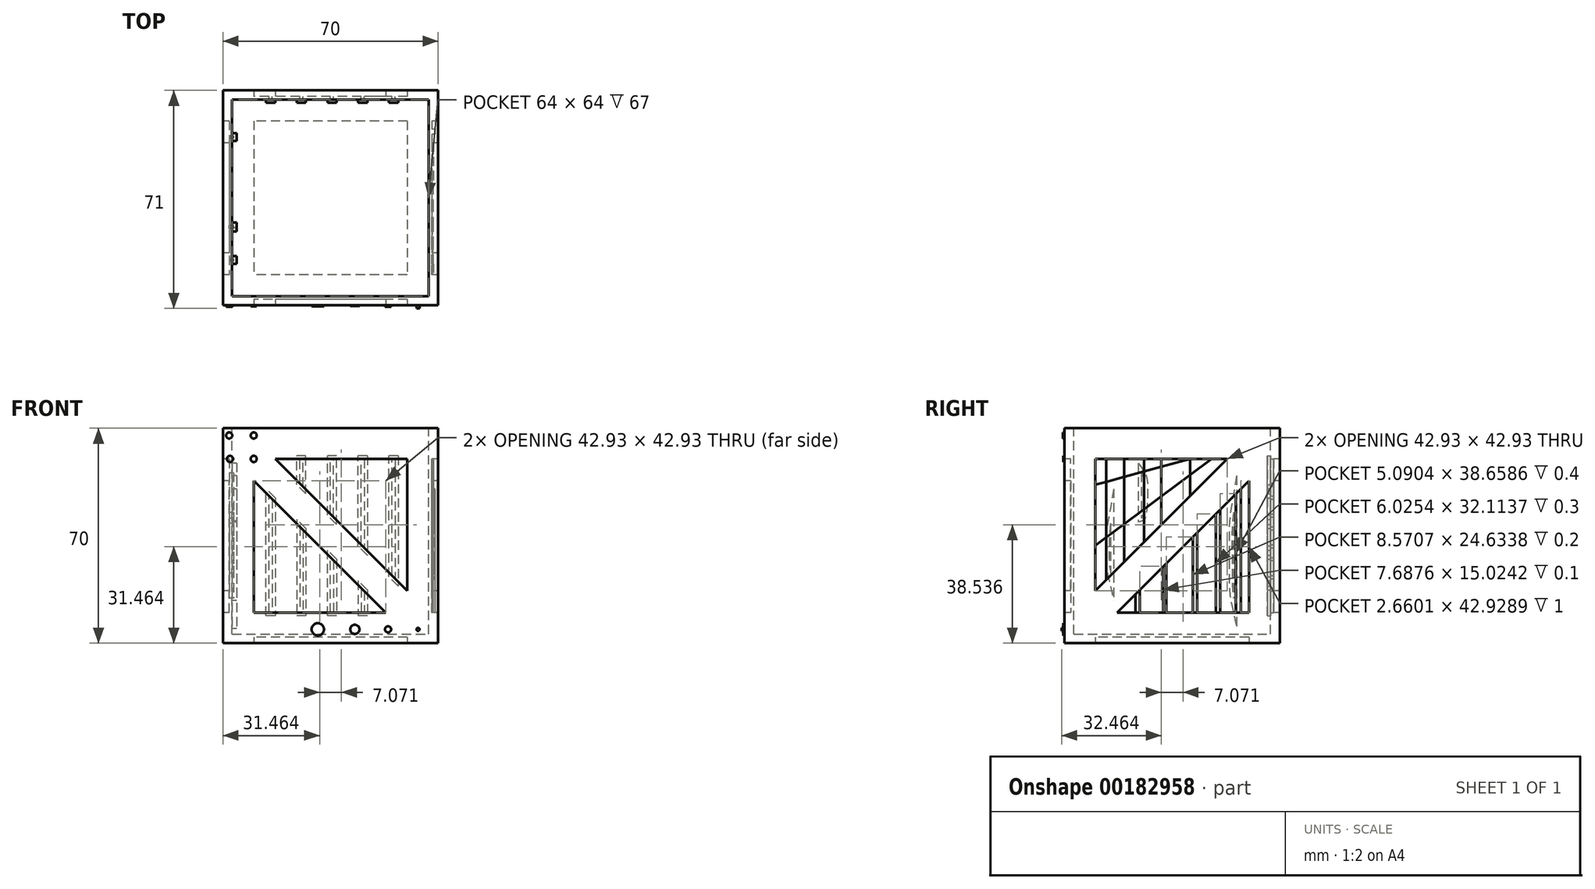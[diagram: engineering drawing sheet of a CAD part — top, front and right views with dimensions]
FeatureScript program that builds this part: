
annotation { "Feature Type Name" : "Feature", "Feature Type Description" : "" }
export const myFeature = defineFeature(function(context is Context, id is Id, definition is map)
    precondition{}
    {
        {
            var Q0;
            Q0=qCreatedBy(makeId("Top.planeOp"),FACE);
            var sketch = newSketch(context, id + "F0", { "sketchPlane" : qUnion([Q0])});
            skLineSegment(sketch, "E0.bottom", {"start": v(35, 35) * mm, "end": v(-35, 35) * mm});
            skLineSegment(sketch, "E0.top", {"start": v(35, -35) * mm, "end": v(-35, -35) * mm});
            skLineSegment(sketch, "E0.left", {"start": v(35, 35) * mm, "end": v(35, -35) * mm});
            skLineSegment(sketch, "E0.right", {"start": v(-35, 35) * mm, "end": v(-35, -35) * mm});
            skPoint(sketch, "E0.middle", {"position": v(0, 0) * mm});
            skLineSegment(sketch, "E1.0", {"start": v(25, 25) * mm, "end": v(-25, 25) * mm});
            skLineSegment(sketch, "E1.1", {"start": v(25, 25) * mm, "end": v(25, -25) * mm});
            skLineSegment(sketch, "E1.2", {"start": v(25, -25) * mm, "end": v(-25, -25) * mm});
            skLineSegment(sketch, "E1.3", {"start": v(-25, 25) * mm, "end": v(-25, -25) * mm});
            skLineSegment(sketch, "E2.0", {"start": v(33, 33) * mm, "end": v(-33, 33) * mm});
            skLineSegment(sketch, "E2.1", {"start": v(33, 33) * mm, "end": v(33, -33) * mm});
            skLineSegment(sketch, "E2.2", {"start": v(33, -33) * mm, "end": v(-33, -33) * mm});
            skLineSegment(sketch, "E2.3", {"start": v(-33, 33) * mm, "end": v(-33, -33) * mm});
            skSolve(sketch);
        }
        {
            var Q0;
            Q0=makeQuery(id+"F0.imprint","IMPRINT",FACE,{"disambiguationData":[TD([[makeQuery(id+"F0.imprint","IMPRINT",EDGE,{"derivedFrom":sQuery(id+"F0.wireOp",EDGE,"E1.0")}),-1.0]])]});
            extrude(context, id + "F1", {"entities" : qUnion([Q0]), "depth" : 2 * mm});
        }
        {
            var Q0;
            Q0=makeQuery(id+"F0.imprint","IMPRINT",FACE,{"disambiguationData":[TD([[makeQuery(id+"F0.imprint","IMPRINT",EDGE,{"derivedFrom":sQuery(id+"F0.wireOp",EDGE,"E0.bottom")}),1.0]])]});
            extrude(context, id + "F2", {"entities" : qUnion([Q0]), "operationType" : NewBodyOperationType.ADD, "depth" : 70 * mm});
        }
        {
            var Q0;
            Q0=makeQuery(id+"F2.opExtrude","SWEPT_FACE",FACE,{"disambiguationData":[OSD([sQuery(id+"F0.wireOp",EDGE,"E0.top")])]});
            var sketch = newSketch(context, id + "F3", { "sketchPlane" : qUnion([Q0])});
            skLineSegment(sketch, "E3.0", {"start": v(35, 0) * mm, "end": v(-35, 0) * mm});
            skLineSegment(sketch, "E4.0", {"start": v(35, 70) * mm, "end": v(35, 0) * mm});
            skLineSegment(sketch, "E5.0", {"start": v(-35, 70) * mm, "end": v(-35, 0) * mm});
            skLineSegment(sketch, "E6.0", {"start": v(35, 70) * mm, "end": v(-35, 70) * mm});
            skLineSegment(sketch, "E7.0", {"start": v(25, 10) * mm, "end": v(-25, 10) * mm});
            skLineSegment(sketch, "E7.1", {"start": v(25, 60) * mm, "end": v(25, 10) * mm});
            skLineSegment(sketch, "E7.2", {"start": v(25, 60) * mm, "end": v(-25, 60) * mm});
            skLineSegment(sketch, "E7.3", {"start": v(-25, 60) * mm, "end": v(-25, 10) * mm});
            skLineSegment(sketch, "E8", {"start": v(35, 0) * mm, "end": v(-35, 70) * mm, "construction": true});
            skLineSegment(sketch, "E9.0", {"start": v(17.93, 10) * mm, "end": v(-25, 52.93) * mm});
            skLineSegment(sketch, "E10.trimOffspring", {"start": v(25, 17.07) * mm, "end": v(-17.93, 60) * mm});
            skSolve(sketch);
        }
        {
            var Q0;
            {var subQ3=sQuery(id+"F3.wireOp",EDGE,"E10.trimOffspring");Q0=makeQuery(id+"F3.imprint","IMPRINT",FACE,{"disambiguationData":[TD([[makeQuery(id+"F3.imprint","IMPRINT",EDGE,{"derivedFrom":subQ3}),-1.0]])]});}
            var Q1;
            {var subQ3=sQuery(id+"F3.wireOp",EDGE,"E9.0");Q1=makeQuery(id+"F3.imprint","IMPRINT",FACE,{"disambiguationData":[TD([[makeQuery(id+"F3.imprint","IMPRINT",EDGE,{"derivedFrom":subQ3}),1.0]])]});}
            extrude(context, id + "F4", {"entities" : qUnion([Q0, Q1]), "operationType" : NewBodyOperationType.REMOVE, "endBound" : BoundingType.THROUGH_ALL, "oppositeDirection" : true, "depth" : 25 * mm});
        }
        {
            var Q0;
            Q0=makeQuery(id+"F2.opExtrude","SWEPT_FACE",FACE,{"disambiguationData":[OSD([sQuery(id+"F0.wireOp",EDGE,"E0.right")])]});
            var sketch = newSketch(context, id + "F5", { "sketchPlane" : qUnion([Q0])});
            skLineSegment(sketch, "E11.0", {"start": v(35, 0) * mm, "end": v(-35, 0) * mm});
            skLineSegment(sketch, "E12.0", {"start": v(35, 70) * mm, "end": v(35, 0) * mm});
            skLineSegment(sketch, "E13.0", {"start": v(-35, 70) * mm, "end": v(-35, 0) * mm});
            skLineSegment(sketch, "E14.0", {"start": v(35, 70) * mm, "end": v(-35, 70) * mm});
            skLineSegment(sketch, "E15.0", {"start": v(25, 10) * mm, "end": v(-25, 10) * mm});
            skLineSegment(sketch, "E15.1", {"start": v(25, 60) * mm, "end": v(25, 10) * mm});
            skLineSegment(sketch, "E15.2", {"start": v(25, 60) * mm, "end": v(-25, 60) * mm});
            skLineSegment(sketch, "E15.3", {"start": v(-25, 60) * mm, "end": v(-25, 10) * mm});
            skLineSegment(sketch, "E16", {"start": v(35, 0) * mm, "end": v(-35, 70) * mm, "construction": true});
            skLineSegment(sketch, "E17.0", {"start": v(17.93, 10) * mm, "end": v(-25, 52.93) * mm});
            skLineSegment(sketch, "E18.trimOffspring", {"start": v(25, 17.07) * mm, "end": v(-17.93, 60) * mm});
            skSolve(sketch);
        }
        {
            var Q0;
            {var subQ3=sQuery(id+"F5.wireOp",EDGE,"E18.trimOffspring");Q0=makeQuery(id+"F5.imprint","IMPRINT",FACE,{"disambiguationData":[TD([[makeQuery(id+"F5.imprint","IMPRINT",EDGE,{"derivedFrom":subQ3}),-1.0]])]});}
            var Q1;
            {var subQ3=sQuery(id+"F5.wireOp",EDGE,"E17.0");Q1=makeQuery(id+"F5.imprint","IMPRINT",FACE,{"disambiguationData":[TD([[makeQuery(id+"F5.imprint","IMPRINT",EDGE,{"derivedFrom":subQ3}),1.0]])]});}
            extrude(context, id + "F6", {"entities" : qUnion([Q0, Q1]), "operationType" : NewBodyOperationType.REMOVE, "endBound" : BoundingType.THROUGH_ALL, "oppositeDirection" : true, "depth" : 25 * mm});
        }
        {
            var Q0;
            Q0=makeQuery(id+"F2.opExtrude","CAP_FACE",FACE,{"disambiguationData":[OSD([sQuery(id+"F0.wireOp",EDGE,"E0.bottom"),sQuery(id+"F0.wireOp",EDGE,"E0.top"),sQuery(id+"F0.wireOp",EDGE,"E0.left"),sQuery(id+"F0.wireOp",EDGE,"E0.right"),sQuery(id+"F0.wireOp",EDGE,"E2.0"),sQuery(id+"F0.wireOp",EDGE,"E2.1"),sQuery(id+"F0.wireOp",EDGE,"E2.2"),sQuery(id+"F0.wireOp",EDGE,"E2.3")])],"isStart":false});
            var sketch = newSketch(context, id + "F7", { "sketchPlane" : qUnion([Q0])});
            skLineSegment(sketch, "E19.0", {"start": v(33, 33) * mm, "end": v(-33, 33) * mm});
            skLineSegment(sketch, "E20.0", {"start": v(-33, 33) * mm, "end": v(-33, -33) * mm});
            skLineSegment(sketch, "E21.0", {"start": v(33, 33) * mm, "end": v(33, -33) * mm});
            skLineSegment(sketch, "E22.0", {"start": v(33, -33) * mm, "end": v(-33, -33) * mm});
            skSolve(sketch);
        }
        {
            var Q0;
            Q0=makeQuery(id+"F7.imprint","IMPRINT",FACE,{"disambiguationData":[TD([[makeQuery(id+"F7.imprint","IMPRINT",EDGE,{"derivedFrom":sQuery(id+"F7.wireOp",EDGE,"E19.0")}),1.0]])]});
            var Q1;
            Q1=makeQuery(id+"F1.opExtrude","CAP_FACE",FACE,{"disambiguationData":[OSD([sQuery(id+"F0.wireOp",EDGE,"E1.0"),sQuery(id+"F0.wireOp",EDGE,"E1.1"),sQuery(id+"F0.wireOp",EDGE,"E1.2"),sQuery(id+"F0.wireOp",EDGE,"E1.3"),sQuery(id+"F0.wireOp",EDGE,"E2.0"),sQuery(id+"F0.wireOp",EDGE,"E2.1"),sQuery(id+"F0.wireOp",EDGE,"E2.2"),sQuery(id+"F0.wireOp",EDGE,"E2.3")])],"isStart":false});
            extrude(context, id + "F8", {"entities" : qUnion([Q0]), "endBound" : BoundingType.UP_TO_SURFACE, "oppositeDirection" : true, "endBoundEntityFace" : qUnion([Q1]), "depth" : 25 * mm});
        }
        {
            var Q0;
            Q0=makeQuery(id+"F8.opExtrude","SWEPT_FACE",FACE,{"disambiguationData":[OSD([sQuery(id+"F7.wireOp",EDGE,"E19.0")])]});
            var sketch = newSketch(context, id + "F9", { "sketchPlane" : qUnion([Q0])});
            skLineSegment(sketch, "E23", {"start": v(0, 2) * mm, "end": v(0, 70) * mm, "construction": true});
            skLineSegment(sketch, "E24", {"start": v(-10, 70) * mm, "end": v(-10, 2) * mm, "construction": true});
            skLineSegment(sketch, "E25", {"start": v(-20, 2) * mm, "end": v(-20, 70) * mm, "construction": true});
            skLineSegment(sketch, "E26", {"start": v(-30, 2) * mm, "end": v(-30, 70) * mm, "construction": true});
            skLineSegment(sketch, "E27.1.0.0", {"start": v(30, 2) * mm, "end": v(30, 70) * mm, "construction": true});
            skLineSegment(sketch, "E27.1.0.1", {"start": v(20, 70) * mm, "end": v(20, 2) * mm, "construction": true});
            skLineSegment(sketch, "E27.direction1", {"start": v(-10, 2) * mm, "end": v(20, 2) * mm, "construction": true});
            skLineSegment(sketch, "E28", {"start": v(10, 2) * mm, "end": v(10, 70) * mm, "construction": true});
            skLineSegment(sketch, "E29.0", {"start": v(-17.93, 10) * mm, "end": v(25, 52.93) * mm});
            skLineSegment(sketch, "E30.0", {"start": v(25, 52.93) * mm, "end": v(25, 10) * mm});
            skLineSegment(sketch, "E31.0", {"start": v(-17.93, 10) * mm, "end": v(25, 10) * mm});
            skLineSegment(sketch, "E32.0", {"start": v(-25, 17.07) * mm, "end": v(17.93, 60) * mm});
            skLineSegment(sketch, "E33.0", {"start": v(-25, 60) * mm, "end": v(-25, 17.07) * mm});
            skLineSegment(sketch, "E34.0", {"start": v(-25, 60) * mm, "end": v(17.93, 60) * mm});
            skLineSegment(sketch, "E35", {"start": v(-10, 32.07) * mm, "end": v(-10, 60) * mm});
            skLineSegment(sketch, "E36", {"start": v(-10, 60) * mm, "end": v(-11, 60) * mm});
            skLineSegment(sketch, "E37", {"start": v(-11, 60) * mm, "end": v(-11, 31.07) * mm});
            skLineSegment(sketch, "E38", {"start": v(0, 42.07) * mm, "end": v(0, 60) * mm});
            skLineSegment(sketch, "E39", {"start": v(-1, 41.07) * mm, "end": v(-1, 60) * mm});
            skLineSegment(sketch, "E40", {"start": v(10, 52.07) * mm, "end": v(10, 60) * mm});
            skLineSegment(sketch, "E41", {"start": v(9, 51.07) * mm, "end": v(9, 60) * mm});
            skLineSegment(sketch, "E42", {"start": v(-20, 22.07) * mm, "end": v(-20, 60) * mm});
            skLineSegment(sketch, "E43", {"start": v(-21, 60) * mm, "end": v(-21, 21.07) * mm});
            skLineSegment(sketch, "E44", {"start": v(-10, 17.93) * mm, "end": v(-10, 10) * mm});
            skLineSegment(sketch, "E45", {"start": v(-11, 16.93) * mm, "end": v(-11, 10) * mm});
            skLineSegment(sketch, "E46", {"start": v(-1, 26.93) * mm, "end": v(-1, 10) * mm});
            skLineSegment(sketch, "E47", {"start": v(0, 10) * mm, "end": v(0, 27.93) * mm});
            skLineSegment(sketch, "E48", {"start": v(10, 37.93) * mm, "end": v(10, 10) * mm});
            skLineSegment(sketch, "E49", {"start": v(9, 36.93) * mm, "end": v(9, 10) * mm});
            skLineSegment(sketch, "E50", {"start": v(20, 10) * mm, "end": v(20, 47.93) * mm});
            skLineSegment(sketch, "E51", {"start": v(19, 46.93) * mm, "end": v(19, 10) * mm});
            skSolve(sketch);
        }
        {
            var Q0;
            {var subQ0=sQuery(id+"F9.wireOp",EDGE,"E35");Q0=makeQuery(id+"F9.imprint","IMPRINT",FACE,{"disambiguationData":[TD([[makeQuery(id+"F9.imprint","IMPRINT",EDGE,{"derivedFrom":subQ0}),1.0]])]});}
            extrude(context, id + "F10", {"entities" : qUnion([Q0]), "operationType" : NewBodyOperationType.REMOVE, "oppositeDirection" : true, "depth" : 1 * mm});
        }
        {
            var Q0;
            {var subQ0=sQuery(id+"F9.wireOp",EDGE,"E42");Q0=makeQuery(id+"F9.imprint","IMPRINT",FACE,{"disambiguationData":[TD([[makeQuery(id+"F9.imprint","IMPRINT",EDGE,{"derivedFrom":subQ0}),1.0]])]});}
            var Q1;
            {var subQ0=sQuery(id+"F9.wireOp",EDGE,"E38");Q1=makeQuery(id+"F9.imprint","IMPRINT",FACE,{"disambiguationData":[TD([[makeQuery(id+"F9.imprint","IMPRINT",EDGE,{"derivedFrom":subQ0}),1.0]])]});}
            var Q2;
            {var subQ0=sQuery(id+"F9.wireOp",EDGE,"E40");Q2=makeQuery(id+"F9.imprint","IMPRINT",FACE,{"disambiguationData":[TD([[makeQuery(id+"F9.imprint","IMPRINT",EDGE,{"derivedFrom":subQ0}),1.0]])]});}
            var Q3;
            {var subQ0=sQuery(id+"F9.wireOp",EDGE,"E50");Q3=makeQuery(id+"F9.imprint","IMPRINT",FACE,{"disambiguationData":[TD([[makeQuery(id+"F9.imprint","IMPRINT",EDGE,{"derivedFrom":subQ0}),1.0]])]});}
            var Q4;
            {var subQ0=sQuery(id+"F9.wireOp",EDGE,"E48");Q4=makeQuery(id+"F9.imprint","IMPRINT",FACE,{"disambiguationData":[TD([[makeQuery(id+"F9.imprint","IMPRINT",EDGE,{"derivedFrom":subQ0}),-1.0]])]});}
            var Q5;
            {var subQ0=sQuery(id+"F9.wireOp",EDGE,"E46");Q5=makeQuery(id+"F9.imprint","IMPRINT",FACE,{"disambiguationData":[TD([[makeQuery(id+"F9.imprint","IMPRINT",EDGE,{"derivedFrom":subQ0}),1.0]])]});}
            var Q6;
            {var subQ0=sQuery(id+"F9.wireOp",EDGE,"E44");Q6=makeQuery(id+"F9.imprint","IMPRINT",FACE,{"disambiguationData":[TD([[makeQuery(id+"F9.imprint","IMPRINT",EDGE,{"derivedFrom":subQ0}),-1.0]])]});}
            extrude(context, id + "F11", {"entities" : qUnion([Q0, Q1, Q2, Q3, Q4, Q5, Q6]), "operationType" : NewBodyOperationType.REMOVE, "oppositeDirection" : true, "depth" : 1 * mm});
        }
        {
            var Q0;
            Q0=makeQuery(id+"F8.opExtrude","SWEPT_FACE",FACE,{"disambiguationData":[OSD([sQuery(id+"F7.wireOp",EDGE,"E20.0")])]});
            var sketch = newSketch(context, id + "F12", { "sketchPlane" : qUnion([Q0])});
            skLineSegment(sketch, "E52.0", {"start": v(17.93, 10) * mm, "end": v(-25, 52.93) * mm});
            skLineSegment(sketch, "E53.0", {"start": v(-25, 52.93) * mm, "end": v(-25, 10) * mm});
            skLineSegment(sketch, "E54.0", {"start": v(17.93, 10) * mm, "end": v(-25, 10) * mm});
            skLineSegment(sketch, "E55.0", {"start": v(25, 17.07) * mm, "end": v(-17.93, 60) * mm});
            skLineSegment(sketch, "E56.0", {"start": v(25, 60) * mm, "end": v(-17.93, 60) * mm});
            skLineSegment(sketch, "E57.0.0", {"start": v(-33, 2) * mm, "end": v(33, 2) * mm});
            skLineSegment(sketch, "E57.0.1", {"start": v(33, 2) * mm, "end": v(33, 70) * mm});
            skLineSegment(sketch, "E57.0.2", {"start": v(33, 70) * mm, "end": v(-33, 70) * mm});
            skLineSegment(sketch, "E57.0.3", {"start": v(-33, 70) * mm, "end": v(-33, 2) * mm});
            skLineSegment(sketch, "E58.0", {"start": v(25, 60) * mm, "end": v(25, 17.07) * mm});
            skLineSegment(sketch, "E59", {"start": v(0, 60) * mm, "end": v(0, 42.07) * mm});
            skLineSegment(sketch, "E60", {"start": v(0, 27.93) * mm, "end": v(0, 10) * mm});
            skLineSegment(sketch, "E61", {"start": v(10, 60) * mm, "end": v(10, 32.07) * mm});
            skLineSegment(sketch, "E62", {"start": v(20, 60) * mm, "end": v(20, 22.07) * mm});
            skLineSegment(sketch, "E63", {"start": v(10, 17.93) * mm, "end": v(10, 10) * mm});
            skLineSegment(sketch, "E64", {"start": v(-10, 60) * mm, "end": v(-10, 52.07) * mm});
            skLineSegment(sketch, "E65", {"start": v(-10, 37.93) * mm, "end": v(-10, 10) * mm});
            skLineSegment(sketch, "E66", {"start": v(-20, 47.93) * mm, "end": v(-20, 10) * mm});
            skFitSpline(sketch, "E67", {"points": [v(10, 55.47) * mm, v(9, 49.98) * mm, v(9.6, 41.45) * mm, v(10, 40.76) * mm], "startDerivative": vector(-7.51, -10.66) * mm, "endDerivative": vector(1.17, -0.36) * mm});
            skFitSpline(sketch, "E68", {"points": [v(20, 39.02) * mm, v(20.5, 32.07) * mm, v(20.5, 27.05) * mm, v(20, 22.78) * mm], "startDerivative": vector(3.4, -18.97) * mm, "endDerivative": vector(-3.2, -14.11) * mm});
            skFitSpline(sketch, "E69", {"points": [v(-20, 42.62) * mm, v(-19.5, 30.64) * mm, v(-19.6, 18.85) * mm, v(-20, 14.66) * mm], "startDerivative": vector(4.84, -28.62) * mm, "endDerivative": vector(-2.5, -12.22) * mm});
            skSolve(sketch);
        }
        {
            var Q0;
            {var subQ0=sQuery(id+"F12.wireOp",EDGE,"E69");Q0=makeQuery(id+"F12.imprint","IMPRINT",FACE,{"disambiguationData":[TD([[makeQuery(id+"F12.imprint","IMPRINT",EDGE,{"derivedFrom":subQ0}),-1.0]])]});}
            var Q1;
            {var subQ0=sQuery(id+"F12.wireOp",EDGE,"E67");Q1=makeQuery(id+"F12.imprint","IMPRINT",FACE,{"disambiguationData":[TD([[makeQuery(id+"F12.imprint","IMPRINT",EDGE,{"derivedFrom":subQ0}),1.0]])]});}
            var Q2;
            {var subQ0=sQuery(id+"F12.wireOp",EDGE,"E68");Q2=makeQuery(id+"F12.imprint","IMPRINT",FACE,{"disambiguationData":[TD([[makeQuery(id+"F12.imprint","IMPRINT",EDGE,{"derivedFrom":subQ0}),-1.0]])]});}
            extrude(context, id + "F13", {"entities" : qUnion([Q0, Q1, Q2]), "operationType" : NewBodyOperationType.REMOVE, "oppositeDirection" : true, "depth" : 1.5 * mm});
        }
        {
            var Q0;
            Q0=makeQuery(id+"F8.opExtrude","CAP_FACE",FACE,{"disambiguationData":[OSD([sQuery(id+"F7.wireOp",EDGE,"E19.0"),sQuery(id+"F7.wireOp",EDGE,"E20.0"),sQuery(id+"F7.wireOp",EDGE,"E21.0"),sQuery(id+"F7.wireOp",EDGE,"E22.0")])],"isStart":true});
            var Q1;
            Q1=makeQuery(id+"F8.opExtrude","SWEPT_BODY",BODY,{"disambiguationData":[OSD([sQuery(id+"F7.wireOp",EDGE,"E19.0"),sQuery(id+"F7.wireOp",EDGE,"E20.0"),sQuery(id+"F7.wireOp",EDGE,"E21.0"),sQuery(id+"F7.wireOp",EDGE,"E22.0")])]});
            shell(context, id + "F14", {"entities" : qUnion([Q0]), "parts" : qUnion([Q1]), "thickness" : 1 * mm});
        }
        {
            var Q0;
            Q0=makeQuery(id+"F1.opExtrude","SWEPT_BODY",BODY,{"disambiguationData":[OSD([sQuery(id+"F0.wireOp",EDGE,"E1.0"),sQuery(id+"F0.wireOp",EDGE,"E1.1"),sQuery(id+"F0.wireOp",EDGE,"E1.2"),sQuery(id+"F0.wireOp",EDGE,"E1.3"),sQuery(id+"F0.wireOp",EDGE,"E2.0"),sQuery(id+"F0.wireOp",EDGE,"E2.1"),sQuery(id+"F0.wireOp",EDGE,"E2.2"),sQuery(id+"F0.wireOp",EDGE,"E2.3")])]});
            var Q1;
            Q1=makeQuery(id+"F8.opExtrude","SWEPT_BODY",BODY,{"disambiguationData":[OSD([sQuery(id+"F7.wireOp",EDGE,"E19.0"),sQuery(id+"F7.wireOp",EDGE,"E20.0"),sQuery(id+"F7.wireOp",EDGE,"E21.0"),sQuery(id+"F7.wireOp",EDGE,"E22.0")])]});
            booleanBodies(context, id + "F15", {"operationType" : BooleanOperationType.UNION, "tools" : qUnion([Q0, Q1])});
        }
        {
            var Q0;
            {var subQ0=makeQuery(id+"F2.opExtrude","SWEPT_FACE",FACE,{"disambiguationData":[OSD([sQuery(id+"F0.wireOp",EDGE,"E0.left")])]});var subQ4=makeQuery(id+"F6.opExtrude","SWEPT_FACE",FACE,{"disambiguationData":[OSD([sQuery(id+"F5.wireOp",EDGE,"E15.1")])]});Q0=makeQuery(id+"F15.opBoolean","SPLIT",FACE,{"disambiguationData":[TD([makeQuery(id+"F6.boolean.opBoolean","COPY",FACE,{"disambiguationData":[TD([subQ0])],"derivedFrom":subQ4})])],"derivedFrom":makeQuery(id+"F8.opExtrude","SWEPT_FACE",FACE,{"disambiguationData":[OSD([sQuery(id+"F7.wireOp",EDGE,"E21.0")])]})});}
            var sketch = newSketch(context, id + "F16", { "sketchPlane" : qUnion([Q0])});
            skLineSegment(sketch, "E70.0.0", {"start": v(-25, 60) * mm, "end": v(-25, 17.07) * mm});
            skLineSegment(sketch, "E70.0.1", {"start": v(-25, 17.07) * mm, "end": v(17.93, 60) * mm});
            skLineSegment(sketch, "E70.0.2", {"start": v(17.93, 60) * mm, "end": v(-25, 60) * mm});
            skLineSegment(sketch, "E71.0.0", {"start": v(-17.93, 10) * mm, "end": v(25, 10) * mm});
            skLineSegment(sketch, "E71.0.1", {"start": v(25, 10) * mm, "end": v(25, 52.93) * mm});
            skLineSegment(sketch, "E71.0.2", {"start": v(25, 52.93) * mm, "end": v(-17.93, 10) * mm});
            skLineSegment(sketch, "E72", {"start": v(-21.46, 60) * mm, "end": v(-21.46, 20.61) * mm});
            skLineSegment(sketch, "E73", {"start": v(-15.64, 60) * mm, "end": v(-15.64, 26.43) * mm});
            skLineSegment(sketch, "E74", {"start": v(-9.2, 60) * mm, "end": v(-9.2, 32.87) * mm});
            skLineSegment(sketch, "E75", {"start": v(-3.54, 60) * mm, "end": v(-3.54, 38.54) * mm});
            skLineSegment(sketch, "E76", {"start": v(5.86, 60) * mm, "end": v(5.86, 47.93) * mm});
            skLineSegment(sketch, "E77", {"start": v(-25, 31.84) * mm, "end": v(12.82, 60) * mm});
            skLineSegment(sketch, "E78", {"start": v(-25, 51.58) * mm, "end": v(5.86, 60) * mm});
            skLineSegment(sketch, "E79", {"start": v(22.34, 50.27) * mm, "end": v(22.34, 10) * mm});
            skLineSegment(sketch, "E80", {"start": v(20.73, 48.66) * mm, "end": v(20.73, 10) * mm});
            skLineSegment(sketch, "E81", {"start": v(15.64, 43.57) * mm, "end": v(15.64, 10) * mm});
            skLineSegment(sketch, "E82", {"start": v(14.18, 42.11) * mm, "end": v(14.18, 10) * mm});
            skLineSegment(sketch, "E83", {"start": v(8.16, 36.09) * mm, "end": v(8.16, 10) * mm});
            skLineSegment(sketch, "E84", {"start": v(6.7, 34.63) * mm, "end": v(6.7, 10) * mm});
            skLineSegment(sketch, "E85", {"start": v(-1.87, 26.06) * mm, "end": v(-1.87, 10) * mm});
            skLineSegment(sketch, "E86", {"start": v(-2.9, 25.02) * mm, "end": v(-2.9, 10) * mm});
            skLineSegment(sketch, "E87", {"start": v(-10.6, 17.34) * mm, "end": v(-10.6, 10) * mm});
            skLineSegment(sketch, "E88", {"start": v(-11.94, 15.99) * mm, "end": v(-11.94, 10) * mm});
            skSolve(sketch);
        }
        {
            var Q0;
            {var subQ0=sQuery(id+"F16.wireOp",EDGE,"E70.0.2");var subQ1=sQuery(id+"F16.wireOp",EDGE,"E70.0.0");var subQ2=makeQuery(id+"F16.imprint","INTERSECT",VERTEX,{"derivedFrom":[subQ1,subQ0]});Q0=makeQuery(id+"F16.imprint","IMPRINT",FACE,{"disambiguationData":[TD([[makeQuery(id+"F16.imprint","IMPRINT",EDGE,{"disambiguationData":[TD([[subQ2,1.0]])],"derivedFrom":subQ1}),-1.0]])]});}
            var Q1;
            {var subQ0=sQuery(id+"F16.wireOp",EDGE,"E78");var subQ1=sQuery(id+"F16.wireOp",EDGE,"E73");var subQ2=makeQuery(id+"F16.imprint","INTERSECT",VERTEX,{"derivedFrom":[subQ1,subQ0]});Q1=makeQuery(id+"F16.imprint","IMPRINT",FACE,{"disambiguationData":[TD([[makeQuery(id+"F16.imprint","IMPRINT",EDGE,{"disambiguationData":[TD([[subQ2,-1.0]])],"derivedFrom":subQ1}),1.0]])]});}
            var Q2;
            {var subQ0=sQuery(id+"F16.wireOp",EDGE,"E72");var subQ1=sQuery(id+"F16.wireOp",EDGE,"E70.0.1");var subQ2=makeQuery(id+"F16.imprint","INTERSECT",VERTEX,{"derivedFrom":[subQ1,subQ0]});Q2=makeQuery(id+"F16.imprint","IMPRINT",FACE,{"disambiguationData":[TD([[makeQuery(id+"F16.imprint","IMPRINT",EDGE,{"disambiguationData":[TD([[subQ2,1.0]])],"derivedFrom":subQ1}),-1.0]])]});}
            var Q3;
            {var subQ0=sQuery(id+"F16.wireOp",EDGE,"E78");var subQ1=sQuery(id+"F16.wireOp",EDGE,"E75");var subQ2=makeQuery(id+"F16.imprint","INTERSECT",VERTEX,{"derivedFrom":[subQ1,subQ0]});Q3=makeQuery(id+"F16.imprint","IMPRINT",FACE,{"disambiguationData":[TD([[makeQuery(id+"F16.imprint","IMPRINT",EDGE,{"disambiguationData":[TD([[subQ2,-1.0]])],"derivedFrom":subQ1}),1.0]])]});}
            var Q4;
            {var subQ0=sQuery(id+"F16.wireOp",EDGE,"E74");var subQ1=sQuery(id+"F16.wireOp",EDGE,"E70.0.2");var subQ2=makeQuery(id+"F16.imprint","INTERSECT",VERTEX,{"derivedFrom":[subQ1,subQ0]});Q4=makeQuery(id+"F16.imprint","IMPRINT",FACE,{"disambiguationData":[TD([[makeQuery(id+"F16.imprint","IMPRINT",EDGE,{"disambiguationData":[TD([[subQ2,1.0]])],"derivedFrom":subQ1}),1.0]])]});}
            var Q5;
            {var subQ0=sQuery(id+"F16.wireOp",EDGE,"E74");var subQ1=sQuery(id+"F16.wireOp",EDGE,"E70.0.1");var subQ2=makeQuery(id+"F16.imprint","INTERSECT",VERTEX,{"derivedFrom":[subQ1,subQ0]});Q5=makeQuery(id+"F16.imprint","IMPRINT",FACE,{"disambiguationData":[TD([[makeQuery(id+"F16.imprint","IMPRINT",EDGE,{"disambiguationData":[TD([[subQ2,1.0]])],"derivedFrom":subQ1}),-1.0]])]});}
            var Q6;
            {var subQ0=sQuery(id+"F16.wireOp",EDGE,"E70.0.2");var subQ1=sQuery(id+"F16.wireOp",EDGE,"E70.0.1");var subQ2=makeQuery(id+"F16.imprint","INTERSECT",VERTEX,{"derivedFrom":[subQ1,subQ0]});Q6=makeQuery(id+"F16.imprint","IMPRINT",FACE,{"disambiguationData":[TD([[makeQuery(id+"F16.imprint","IMPRINT",EDGE,{"disambiguationData":[TD([[subQ2,-1.0]])],"derivedFrom":subQ1}),-1.0]])]});}
            extrude(context, id + "F17", {"entities" : qUnion([Q0, Q1, Q2, Q3, Q4, Q5, Q6]), "depth" : 0.5 * mm});
        }
        {
            var Q0;
            {var subQ0=sQuery(id+"F16.wireOp",EDGE,"E72");var subQ1=sQuery(id+"F16.wireOp",EDGE,"E70.0.2");var subQ2=makeQuery(id+"F16.imprint","INTERSECT",VERTEX,{"derivedFrom":[subQ1,subQ0]});Q0=makeQuery(id+"F16.imprint","IMPRINT",FACE,{"disambiguationData":[TD([[makeQuery(id+"F16.imprint","IMPRINT",EDGE,{"disambiguationData":[TD([[subQ2,1.0]])],"derivedFrom":subQ1}),1.0]])]});}
            var Q1;
            {var subQ0=sQuery(id+"F16.wireOp",EDGE,"E77");var subQ1=sQuery(id+"F16.wireOp",EDGE,"E70.0.0");var subQ2=makeQuery(id+"F16.imprint","INTERSECT",VERTEX,{"derivedFrom":[subQ1,subQ0]});Q1=makeQuery(id+"F16.imprint","IMPRINT",FACE,{"disambiguationData":[TD([[makeQuery(id+"F16.imprint","IMPRINT",EDGE,{"disambiguationData":[TD([[subQ2,-1.0]])],"derivedFrom":subQ1}),-1.0]])]});}
            var Q2;
            {var subQ0=sQuery(id+"F16.wireOp",EDGE,"E73");var subQ1=sQuery(id+"F16.wireOp",EDGE,"E70.0.1");var subQ2=makeQuery(id+"F16.imprint","INTERSECT",VERTEX,{"derivedFrom":[subQ1,subQ0]});Q2=makeQuery(id+"F16.imprint","IMPRINT",FACE,{"disambiguationData":[TD([[makeQuery(id+"F16.imprint","IMPRINT",EDGE,{"disambiguationData":[TD([[subQ2,1.0]])],"derivedFrom":subQ1}),-1.0]])]});}
            var Q3;
            {var subQ0=sQuery(id+"F16.wireOp",EDGE,"E78");var subQ1=sQuery(id+"F16.wireOp",EDGE,"E74");var subQ2=makeQuery(id+"F16.imprint","INTERSECT",VERTEX,{"derivedFrom":[subQ1,subQ0]});Q3=makeQuery(id+"F16.imprint","IMPRINT",FACE,{"disambiguationData":[TD([[makeQuery(id+"F16.imprint","IMPRINT",EDGE,{"disambiguationData":[TD([[subQ2,-1.0]])],"derivedFrom":subQ1}),1.0]])]});}
            var Q4;
            {var subQ0=sQuery(id+"F16.wireOp",EDGE,"E75");var subQ1=sQuery(id+"F16.wireOp",EDGE,"E70.0.2");var subQ2=makeQuery(id+"F16.imprint","INTERSECT",VERTEX,{"derivedFrom":[subQ1,subQ0]});Q4=makeQuery(id+"F16.imprint","IMPRINT",FACE,{"disambiguationData":[TD([[makeQuery(id+"F16.imprint","IMPRINT",EDGE,{"disambiguationData":[TD([[subQ2,-1.0]])],"derivedFrom":subQ0}),1.0]])]});}
            var Q5;
            {var subQ0=sQuery(id+"F16.wireOp",EDGE,"E75");var subQ1=sQuery(id+"F16.wireOp",EDGE,"E70.0.1");var subQ2=makeQuery(id+"F16.imprint","INTERSECT",VERTEX,{"derivedFrom":[subQ1,subQ0]});Q5=makeQuery(id+"F16.imprint","IMPRINT",FACE,{"disambiguationData":[TD([[makeQuery(id+"F16.imprint","IMPRINT",EDGE,{"disambiguationData":[TD([[subQ2,1.0]])],"derivedFrom":subQ1}),-1.0]])]});}
            extrude(context, id + "F18", {"entities" : qUnion([Q0, Q1, Q2, Q3, Q4, Q5]), "depth" : 0.25 * mm});
        }
        {
            var Q0;
            {var subQ0=sQuery(id+"F16.wireOp",EDGE,"E87");Q0=makeQuery(id+"F16.imprint","IMPRINT",FACE,{"disambiguationData":[TD([[makeQuery(id+"F16.imprint","IMPRINT",EDGE,{"derivedFrom":subQ0}),-1.0]])]});}
            extrude(context, id + "F19", {"entities" : qUnion([Q0]), "operationType" : NewBodyOperationType.ADD, "depth" : 0.1 * mm});
        }
        {
            var Q0;
            {var subQ0=sQuery(id+"F16.wireOp",EDGE,"E85");Q0=makeQuery(id+"F16.imprint","IMPRINT",FACE,{"disambiguationData":[TD([[makeQuery(id+"F16.imprint","IMPRINT",EDGE,{"derivedFrom":subQ0}),-1.0]])]});}
            extrude(context, id + "F20", {"entities" : qUnion([Q0]), "operationType" : NewBodyOperationType.ADD, "depth" : 0.2 * mm});
        }
        {
            var Q0;
            {var subQ0=sQuery(id+"F16.wireOp",EDGE,"E83");Q0=makeQuery(id+"F16.imprint","IMPRINT",FACE,{"disambiguationData":[TD([[makeQuery(id+"F16.imprint","IMPRINT",EDGE,{"derivedFrom":subQ0}),-1.0]])]});}
            extrude(context, id + "F21", {"entities" : qUnion([Q0]), "operationType" : NewBodyOperationType.ADD, "depth" : 0.3 * mm});
        }
        {
            var Q0;
            {var subQ0=sQuery(id+"F16.wireOp",EDGE,"E81");Q0=makeQuery(id+"F16.imprint","IMPRINT",FACE,{"disambiguationData":[TD([[makeQuery(id+"F16.imprint","IMPRINT",EDGE,{"derivedFrom":subQ0}),-1.0]])]});}
            extrude(context, id + "F22", {"entities" : qUnion([Q0]), "operationType" : NewBodyOperationType.ADD, "depth" : 0.4 * mm});
        }
        {
            var Q0;
            {var subQ0=sQuery(id+"F16.wireOp",EDGE,"E79");Q0=makeQuery(id+"F16.imprint","IMPRINT",FACE,{"disambiguationData":[TD([[makeQuery(id+"F16.imprint","IMPRINT",EDGE,{"derivedFrom":subQ0}),-1.0]])]});}
            extrude(context, id + "F23", {"entities" : qUnion([Q0]), "operationType" : NewBodyOperationType.ADD, "depth" : 1 * mm});
        }
        {
            var Q0;
            Q0=makeQuery(id+"F2.opExtrude","SWEPT_FACE",FACE,{"disambiguationData":[OSD([sQuery(id+"F0.wireOp",EDGE,"E0.top")])]});
            var sketch = newSketch(context, id + "F24", { "sketchPlane" : qUnion([Q0])});
            skCircle(sketch, "E89", {"center": v(-25, 60) * mm, "radius": 1 * mm});
            skCircle(sketch, "E90", {"center": v(-25, 67.62) * mm, "radius": 1 * mm});
            skCircle(sketch, "E91", {"center": v(-32.99, 67.62) * mm, "radius": 1 * mm});
            skCircle(sketch, "E92", {"center": v(-32.7, 60) * mm, "radius": 1 * mm});
            skCircle(sketch, "E93", {"center": v(28.47, 4.51) * mm, "radius": 0.5 * mm});
            skCircle(sketch, "E94", {"center": v(18.73, 4.51) * mm, "radius": 1 * mm});
            skCircle(sketch, "E95", {"center": v(7.92, 4.51) * mm, "radius": 1.5 * mm});
            skCircle(sketch, "E96", {"center": v(-4.13, 4.51) * mm, "radius": 2 * mm});
            skSolve(sketch);
        }
        {
            var Q0;
            Q0=makeQuery(id+"F24.imprint","IMPRINT",FACE,{"disambiguationData":[TD([[makeQuery(id+"F24.imprint","IMPRINT",EDGE,{"derivedFrom":sQuery(id+"F24.wireOp",EDGE,"E93")}),1.0]])]});
            extrude(context, id + "F25", {"entities" : qUnion([Q0]), "operationType" : NewBodyOperationType.ADD, "depth" : 1 * mm});
        }
        {
            var Q0;
            Q0=makeQuery(id+"F24.imprint","IMPRINT",FACE,{"disambiguationData":[TD([[makeQuery(id+"F24.imprint","IMPRINT",EDGE,{"derivedFrom":sQuery(id+"F24.wireOp",EDGE,"E94")}),1.0]])]});
            extrude(context, id + "F26", {"entities" : qUnion([Q0]), "operationType" : NewBodyOperationType.ADD, "depth" : 0.5 * mm});
        }
        {
            var Q0;
            Q0=makeQuery(id+"F24.imprint","IMPRINT",FACE,{"disambiguationData":[TD([[makeQuery(id+"F24.imprint","IMPRINT",EDGE,{"derivedFrom":sQuery(id+"F24.wireOp",EDGE,"E95")}),1.0]])]});
            extrude(context, id + "F27", {"entities" : qUnion([Q0]), "operationType" : NewBodyOperationType.ADD, "depth" : 0.2 * mm});
        }
        {
            var Q0;
            Q0=makeQuery(id+"F24.imprint","IMPRINT",FACE,{"disambiguationData":[TD([[makeQuery(id+"F24.imprint","IMPRINT",EDGE,{"derivedFrom":sQuery(id+"F24.wireOp",EDGE,"E96")}),1.0]])]});
            extrude(context, id + "F28", {"entities" : qUnion([Q0]), "operationType" : NewBodyOperationType.ADD, "depth" : 0.4 * mm});
        }
        {
            var Q0;
            Q0=makeQuery(id+"F24.imprint","IMPRINT",FACE,{"disambiguationData":[TD([[makeQuery(id+"F24.imprint","IMPRINT",EDGE,{"derivedFrom":sQuery(id+"F24.wireOp",EDGE,"E91")}),1.0]])]});
            extrude(context, id + "F29", {"entities" : qUnion([Q0]), "operationType" : NewBodyOperationType.ADD, "depth" : 0.5 * mm});
        }
        {
            var Q0;
            Q0=makeQuery(id+"F24.imprint","IMPRINT",FACE,{"disambiguationData":[TD([[makeQuery(id+"F24.imprint","IMPRINT",EDGE,{"derivedFrom":sQuery(id+"F24.wireOp",EDGE,"E90")}),1.0]])]});
            extrude(context, id + "F30", {"entities" : qUnion([Q0]), "operationType" : NewBodyOperationType.ADD, "depth" : 0.2 * mm});
        }
        {
            var Q0;
            Q0=makeQuery(id+"F24.imprint","IMPRINT",FACE,{"disambiguationData":[TD([[makeQuery(id+"F24.imprint","IMPRINT",EDGE,{"derivedFrom":sQuery(id+"F24.wireOp",EDGE,"E92")}),1.0]])]});
            extrude(context, id + "F31", {"entities" : qUnion([Q0]), "operationType" : NewBodyOperationType.ADD, "depth" : 0.25 * mm});
        }
        {
            var Q0;
            Q0=makeQuery(id+"F24.imprint","IMPRINT",FACE,{"disambiguationData":[TD([[makeQuery(id+"F24.imprint","IMPRINT",EDGE,{"derivedFrom":sQuery(id+"F24.wireOp",EDGE,"E89")}),1.0]])]});
            extrude(context, id + "F32", {"entities" : qUnion([Q0]), "operationType" : NewBodyOperationType.ADD, "depth" : 0.4 * mm});
        }
    });
